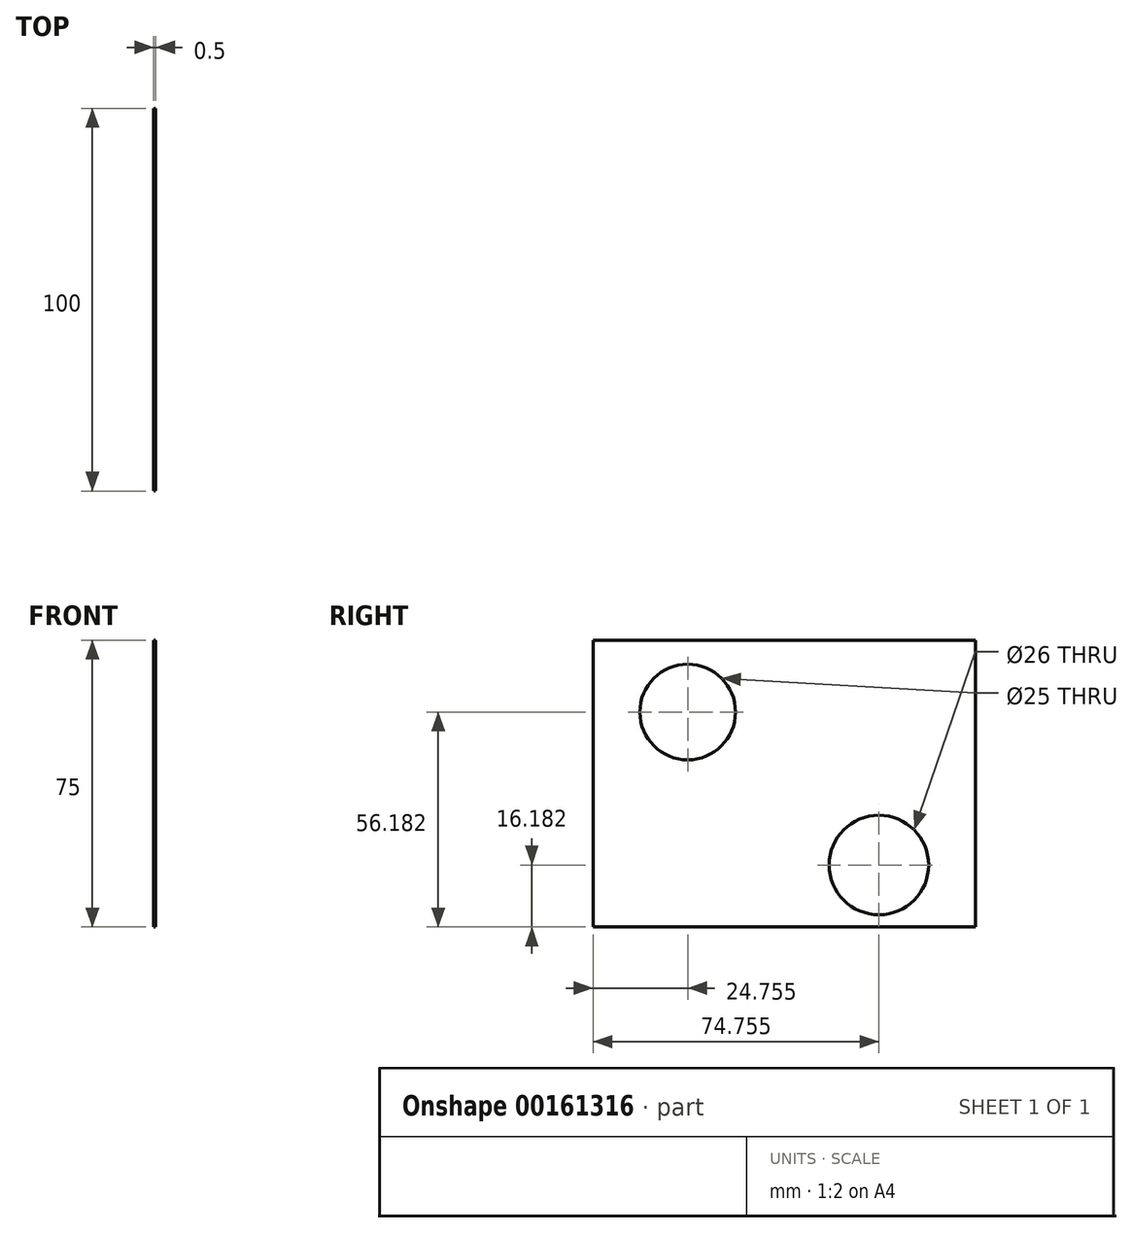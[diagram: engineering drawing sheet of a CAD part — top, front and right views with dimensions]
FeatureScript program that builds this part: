
annotation { "Feature Type Name" : "Feature", "Feature Type Description" : "" }
export const myFeature = defineFeature(function(context is Context, id is Id, definition is map)
    precondition{}
    {
        {
            var Q0;
            Q0=qCreatedBy(makeId("Right.planeOp"),FACE);
            var sketch = newSketch(context, id + "F0", { "sketchPlane" : qUnion([Q0])});
            skLineSegment(sketch, "E0", {"start": v(49.38, 37.05) * mm, "end": v(49.38, -37.95) * mm});
            skCircle(sketch, "E1", {"center": v(24.13, -21.77) * mm, "radius": 13 * mm});
            skCircle(sketch, "E2", {"center": v(-25.87, 18.23) * mm, "radius": 12.5 * mm});
            skLineSegment(sketch, "E3", {"start": v(-50.62, 37.05) * mm, "end": v(49.38, 37.05) * mm});
            skLineSegment(sketch, "E4", {"start": v(-50.62, -37.95) * mm, "end": v(49.38, -37.95) * mm});
            skLineSegment(sketch, "E5", {"start": v(-50.62, 37.05) * mm, "end": v(-50.62, -37.95) * mm});
            skSolve(sketch);
        }
        {
            var Q0;
            Q0 = qSketchRegion(id + "F0", true);
            extrude(context, id + "F1", {"entities" : qUnion([Q0]), "endBound" : BoundingType.SYMMETRIC, "depth" : .5 * mm});
        }
    });
